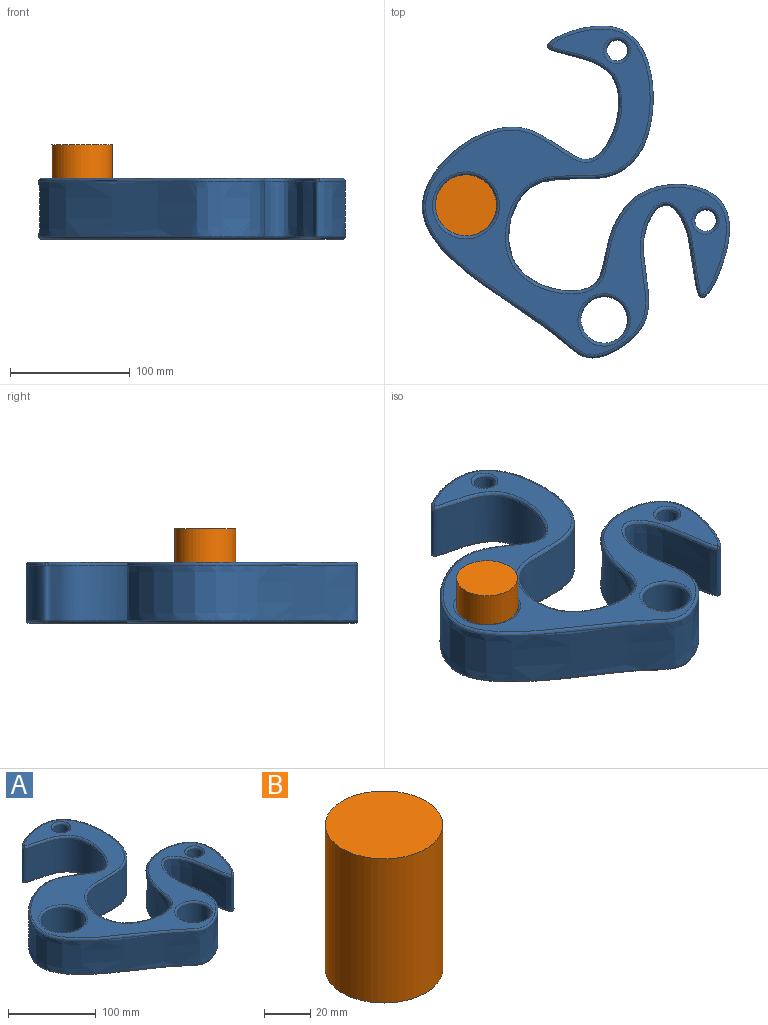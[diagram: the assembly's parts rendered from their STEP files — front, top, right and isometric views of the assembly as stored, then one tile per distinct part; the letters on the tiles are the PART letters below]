
ASSEMBLY  parts=2 mates=1
PART A: 23 faces, bbox 256x276.7x50.8 mm
  f0: cylinder r=25.4mm len=50.8mm, axis (0,0,-1), area 7296.6mm2, adj f10,f14
  f1: cylinder r=19.31mm len=45.72mm, axis (0,0,-1), area 5547.4mm2, adj f9,f13
  f2: cylinder r=8.9mm len=45.72mm, axis (0,0,-1), area 2556.7mm2, adj f8,f12
  f3: cylinder r=8.6mm len=45.72mm, axis (0,0,-1), area 2470.7mm2, adj f7,f11
  f4: extruded ~276.04x249.39mm, area 63002.5mm2, adj f15,f16,f17,f18,f19,f20,f21,f22
  f5: plane 271.66x250.93mm, normal (0,0,1), area 16589.2mm2, adj f11,f12,f13,f14,f20,f21
  f6: plane 271.66x250.94mm, normal (0,0,-1), area 16651.6mm2, adj f7,f8,f9,f10,f16,f17
  f7: torus R=11.14mm, axis (0,0,1), area 238.7mm2, adj f3,f6
  f8: torus R=11.44mm, axis (0,0,1), area 246.2mm2, adj f2,f6
  f9: torus R=21.85mm, axis (0,0,1), area 507.2mm2, adj f1,f6
  f10: torus R=27.94mm, axis (0,0,1), area 659.9mm2, adj f0,f6
  f11: torus R=11.14mm, axis (0,0,1), area 238.7mm2, adj f3,f5
  f12: torus R=11.44mm, axis (0,0,1), area 246.2mm2, adj f2,f5
  f13: torus R=21.85mm, axis (0,0,1), area 507.2mm2, adj f1,f5
  f14: torus R=27.94mm, axis (0,0,1), area 659.9mm2, adj f0,f5
  f15: bspline ~2.58x2.54mm, area 4.3mm2, adj f4,f16,f17
  f16: bspline ~260.14x233.38mm, area 3030.4mm2, adj f4,f6,f15,f18
  f17: bspline ~226.59x186.99mm, area 2668.1mm2, adj f4,f6,f15,f18
  f18: bspline ~2.77x2.61mm, area 4.8mm2, adj f4,f16,f17
  f19: bspline ~2.58x2.54mm, area 4.3mm2, adj f4,f20,f21
  f20: bspline ~260.03x233.38mm, area 3031.4mm2, adj f4,f5,f19,f22
  f21: bspline ~226.59x186.99mm, area 2668.1mm2, adj f4,f5,f19,f22
  f22: bspline ~2.77x2.61mm, area 4.8mm2, adj f4,f20,f21
PART B: 3 faces, bbox 50.8x50.8x76.2 mm
  f0: cylinder r=25.4mm len=76.2mm, axis (0,0,1), area 12161mm2, adj f1,f2
  f1: plane 50.8x50.8mm, normal (0,0,-1), area 2026.8mm2, adj f0
  f2: plane 50.8x50.8mm, normal (0,0,1), area 2026.8mm2, adj f0
PLACE A t=(-131.5,141.7,-81.29)mm
PLACE B t=(-296.61,419.67,9.47)mm
MATE cylindrical B.f0 <-> A.f0  axis (0,0,-1) through (-296.61,164.95,-78.75)mm
